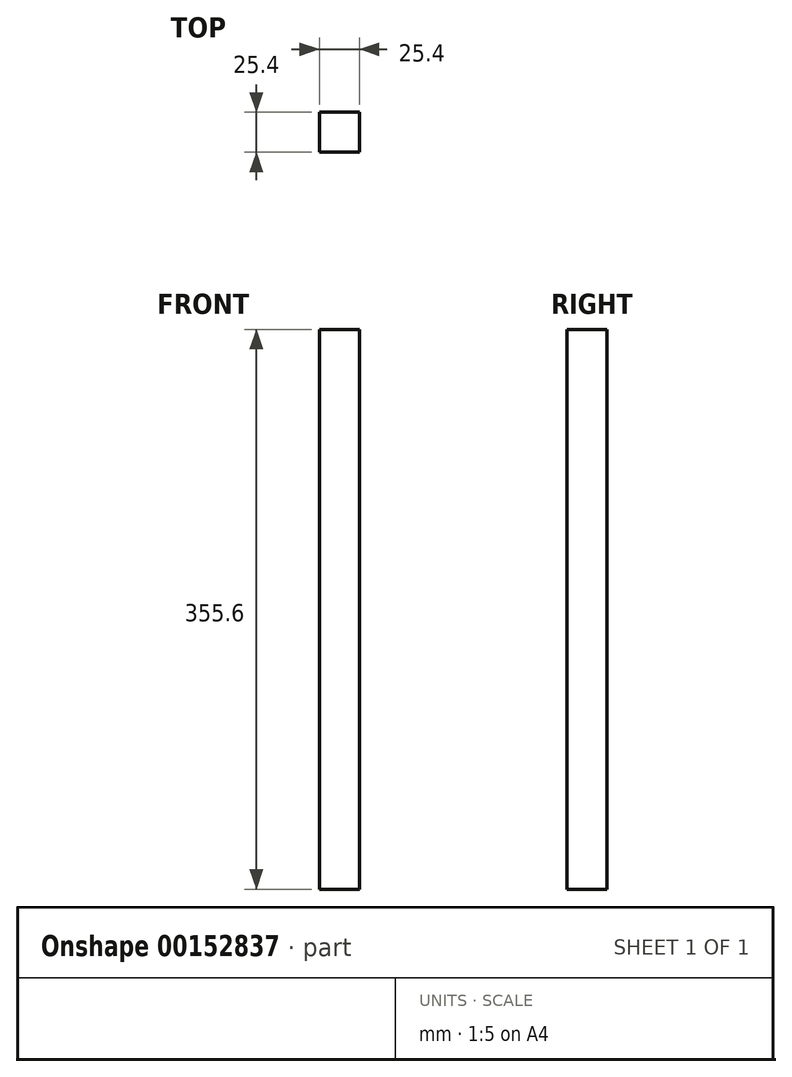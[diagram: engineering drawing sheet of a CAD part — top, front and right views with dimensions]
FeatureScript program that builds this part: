
annotation { "Feature Type Name" : "Feature", "Feature Type Description" : "" }
export const myFeature = defineFeature(function(context is Context, id is Id, definition is map)
    precondition{}
    {
        {
            var Q0;
            Q0=qCreatedBy(makeId("Top.planeOp"),FACE);
            var sketch = newSketch(context, id + "F0", { "sketchPlane" : qUnion([Q0])});
            skLineSegment(sketch, "E0.bottom", {"start": v(12.7, -12.7) * mm, "end": v(-12.7, -12.7) * mm});
            skLineSegment(sketch, "E0.top", {"start": v(12.7, 12.7) * mm, "end": v(-12.7, 12.7) * mm});
            skLineSegment(sketch, "E0.left", {"start": v(12.7, -12.7) * mm, "end": v(12.7, 12.7) * mm});
            skLineSegment(sketch, "E0.right", {"start": v(-12.7, -12.7) * mm, "end": v(-12.7, 12.7) * mm});
            skPoint(sketch, "E0.middle", {"position": v(0, 0) * mm});
            skSolve(sketch);
        }
        {
            var Q0;
            Q0=qSketchRegion(id+"F0",true);
            extrude(context, id + "F1", {"entities" : qUnion([Q0]), "depth" : 355.6 * mm});
        }
    });
